# Revit family: HL_Трап для внутренних помещений_HL310NG
name_source: partatom
category: Instalační zařizovací předměty
revit_build: Autodesk Revit 2016 (Build: 20151007_0715(x64)
units: mm (PartAtom-declared; Revit-internal decimal feet)

## family parameters
Bod výpočtu místnosti = Ano
Kóta kulaté spojky = Použít průměr
Nadpis OmniClass = Deck Waste Water Drains
Ořezat dutým tvarem při načtení = Ne
Sdílené = Ano
Typ součásti = Normální
Vždy vertikální = Ano
Založené na pracovní rovině = Ne
Číslo OmniClass = 23.70.50.21.24.14

## types (1)
- HL310NG
    EAN = 9003076004652
    Klíčová poznámka = HL310NG
    Komentáře k typům = HL310NG Трап для внутренних помещений DN50/75/110 вертикальный 150х150мм/137х137мм чугун.
    Model = HL310NG
    Popis = Трапы для внутренних помещений
    Připojení CW = Ne
    Připojení HW = Ne
    Připojení odpadu = Ano
    Připojení ventilace = Ne
    URL = http://www.hutterer-lechner.com
    Výrobce = HL Hutterer & Lechner GmbH
    ВЕС = 2,40 [kg]
    ВЫСОТА МОНТАЖА = 179 mm
    МАКСИМАЛЬНАЯ НАГРУЗКА КЛАССА = A/L15 - 1,5 t
    МАТЕРИАЛ = PE
    НАСАДКА = 137 x 137 mm / GJL
    ПРОИЗВОДИТЕЛЬНОСТЬ = 0,67 l/s
    ПРОПУСКНАЯ СПОСОБНОСТЬ = 0.7 L/s
    РАЗМЕР = DN50/75/110
    РЕШЁТКА = 35-75 mm / 150 x 150 mm / GJL

## geometry (parser evidence)
native form markers: Sweep x36
no freeform markers — native parametric forms only
